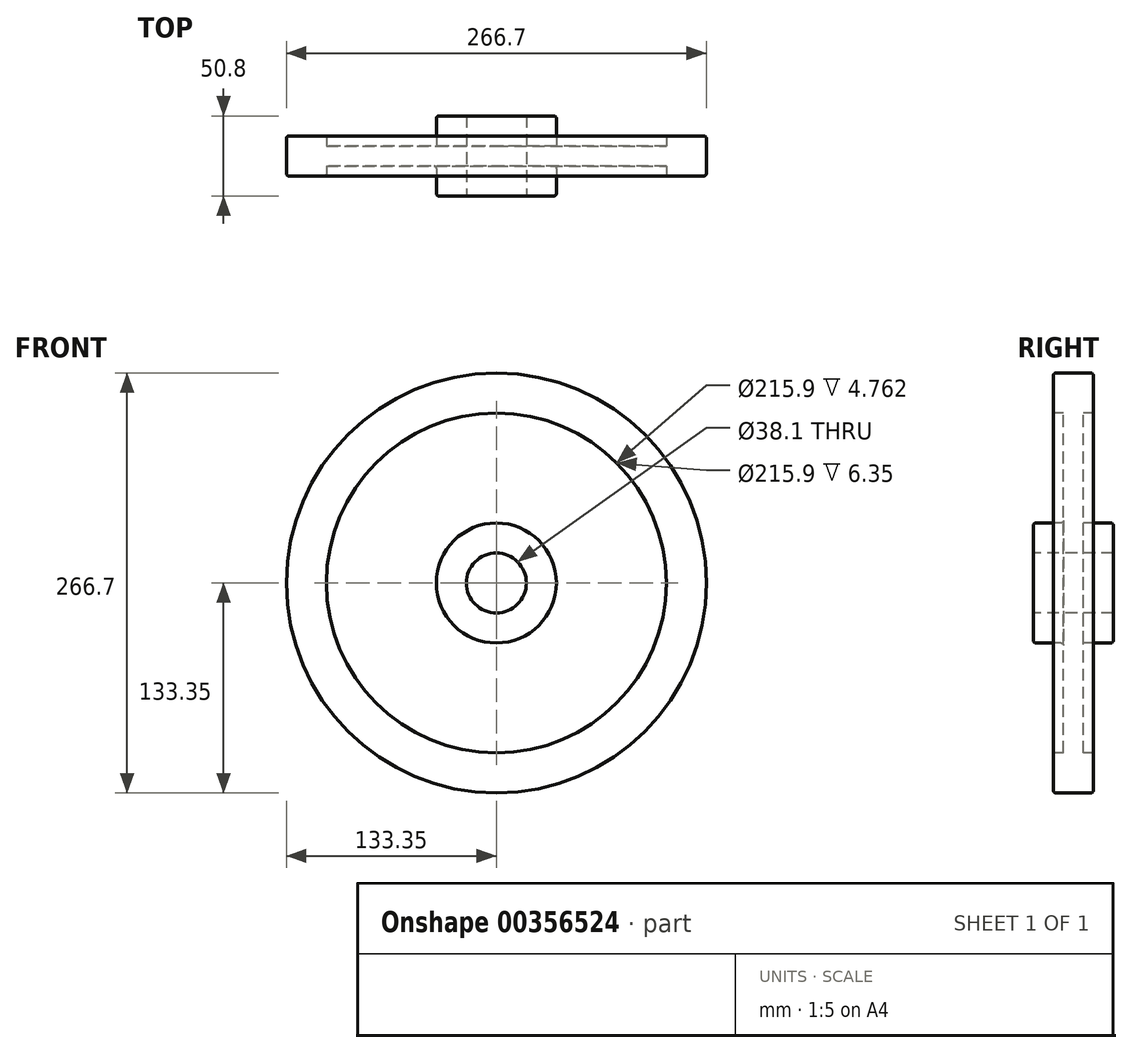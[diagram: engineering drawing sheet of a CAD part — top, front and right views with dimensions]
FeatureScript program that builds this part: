
annotation { "Feature Type Name" : "Feature", "Feature Type Description" : "" }
export const myFeature = defineFeature(function(context is Context, id is Id, definition is map)
    precondition{}
    {
        {
            var Q0;
            Q0=qCreatedBy(makeId("Right.planeOp"),FACE);
            var sketch = newSketch(context, id + "F0", { "sketchPlane" : qUnion([Q0])});
            skLineSegment(sketch, "E0", {"start": v(0, 0) * mm, "end": v(74.98, 0) * mm});
            skLineSegment(sketch, "E1.0", {"start": v(0, 19.05) * mm, "end": v(25.4, 19.05) * mm});
            skLineSegment(sketch, "E2.0", {"start": v(6.35, 38.1) * mm, "end": v(25.4, 38.1) * mm});
            skLineSegment(sketch, "E3.0", {"start": v(6.35, 107.95) * mm, "end": v(12.7, 107.95) * mm});
            skLineSegment(sketch, "E4.0", {"start": v(0, 133.35) * mm, "end": v(12.7, 133.35) * mm});
            skLineSegment(sketch, "E5", {"start": v(0, 0) * mm, "end": v(0, 133.35) * mm, "construction": true});
            skLineSegment(sketch, "E6.MirrorCS", {"start": v(0, 133.35) * mm, "end": v(-12.7, 133.35) * mm});
            skLineSegment(sketch, "E7.MirrorCS", {"start": v(-6.35, 107.95) * mm, "end": v(-12.7, 107.95) * mm});
            skLineSegment(sketch, "E8.MirrorCS", {"start": v(-6.35, 38.1) * mm, "end": v(-25.4, 38.1) * mm});
            skLineSegment(sketch, "E9.MirrorCS", {"start": v(0, 19.05) * mm, "end": v(-25.4, 19.05) * mm});
            skLineSegment(sketch, "E10", {"start": v(6.35, 107.95) * mm, "end": v(6.35, 38.1) * mm});
            skLineSegment(sketch, "E11", {"start": v(-12.7, 133.35) * mm, "end": v(-12.7, 107.95) * mm});
            skLineSegment(sketch, "E12", {"start": v(12.7, 107.95) * mm, "end": v(12.7, 133.35) * mm});
            skLineSegment(sketch, "E13", {"start": v(-6.35, 107.95) * mm, "end": v(-6.35, 38.1) * mm});
            skLineSegment(sketch, "E14", {"start": v(-25.4, 38.1) * mm, "end": v(-25.4, 19.05) * mm});
            skLineSegment(sketch, "E15", {"start": v(25.4, 38.1) * mm, "end": v(25.4, 19.05) * mm});
            skSolve(sketch);
        }
        {
            var Q0;
            Q0 = qSketchRegion(id + "F0", true);
            var Q1;
            Q1=sQuery(id+"F0.wireOp",EDGE,"E0");
            revolve(context, id + "F1", {"entities" : qUnion([Q0]), "axis" : qUnion([Q1]), "revolveType" : RevolveType.FULL});
        }
        {
            var Q0;
            Q0=makeQuery(id+"F1.opRevolve","SWEPT_FACE",FACE,{"disambiguationData":[OSD([sQuery(id+"F0.wireOp",EDGE,"E4.0"),sQuery(id+"F0.wireOp",EDGE,"E6.MirrorCS")])]});
            var Q1;
            Q1=makeQuery(id+"F1.opRevolve","SWEPT_EDGE",EDGE,{"disambiguationData":[OSD([sQuery(id+"F0.wireOp",EDGE,"E6.MirrorCS"),sQuery(id+"F0.wireOp",EDGE,"E11")])]});
            var Q2;
            Q2=makeQuery(id+"F1.opRevolve","SWEPT_EDGE",EDGE,{"disambiguationData":[OSD([sQuery(id+"F0.wireOp",EDGE,"E7.MirrorCS"),sQuery(id+"F0.wireOp",EDGE,"E11")])]});
            var Q3;
            Q3=makeQuery(id+"F1.opRevolve","SWEPT_EDGE",EDGE,{"disambiguationData":[OSD([sQuery(id+"F0.wireOp",EDGE,"E8.MirrorCS"),sQuery(id+"F0.wireOp",EDGE,"E14")])]});
            var Q4;
            Q4=makeQuery(id+"F1.opRevolve","SWEPT_EDGE",EDGE,{"disambiguationData":[OSD([sQuery(id+"F0.wireOp",EDGE,"E2.0"),sQuery(id+"F0.wireOp",EDGE,"E15")])]});
            var Q5;
            Q5=makeQuery(id+"F1.opRevolve","SWEPT_FACE",FACE,{"disambiguationData":[OSD([sQuery(id+"F0.wireOp",EDGE,"E8.MirrorCS")])]});
            fillet(context, id + "F2", {"entities" : qUnion([Q0, Q1, Q2, Q3, Q4, Q5]), "radius" : 1.59 * mm, "tangentPropagation" : true, "allowEdgeOverflow" : false});
        }
    });
